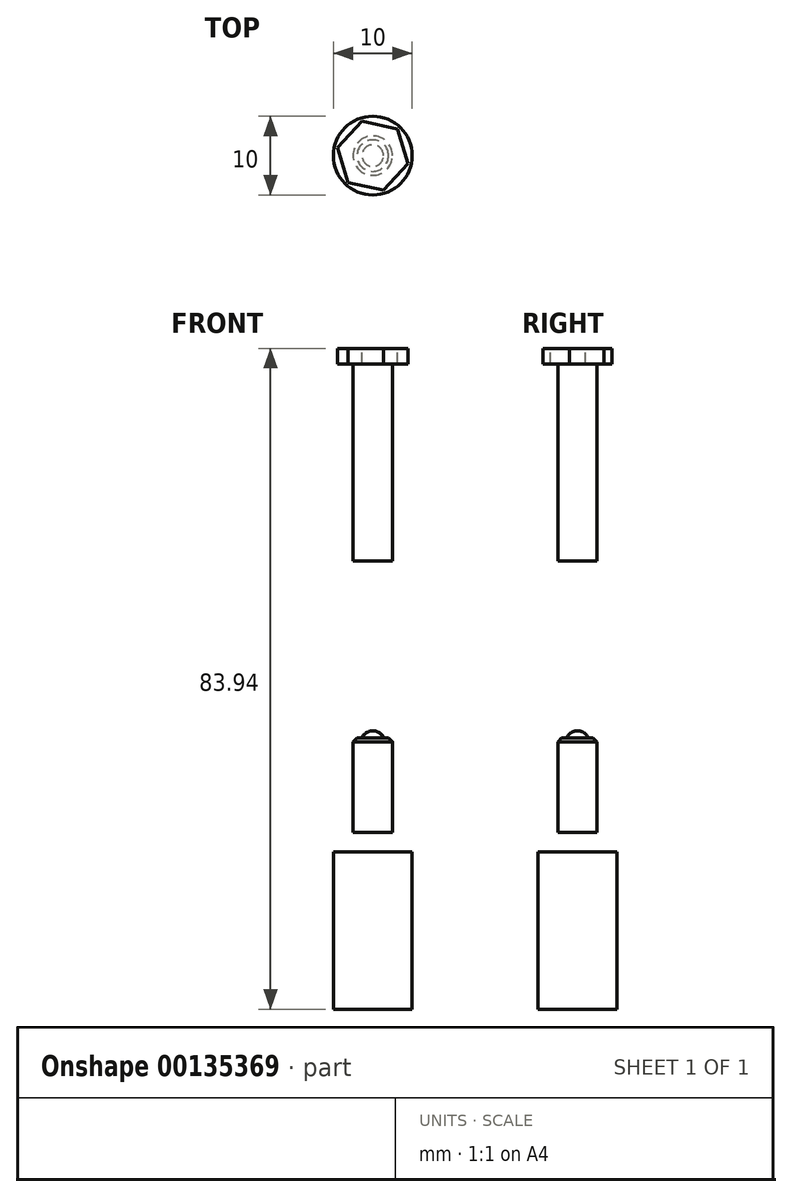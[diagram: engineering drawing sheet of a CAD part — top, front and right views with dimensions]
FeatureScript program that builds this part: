
annotation { "Feature Type Name" : "Feature", "Feature Type Description" : "" }
export const myFeature = defineFeature(function(context is Context, id is Id, definition is map)
    precondition{}
    {
        {
            var Q0;
            Q0=qCreatedBy(makeId("Front.planeOp"),FACE);
            var sketch = newSketch(context, id + "F0", { "sketchPlane" : qUnion([Q0])});
            skLineSegment(sketch, "E0", {"start": v(0, 0) * mm, "end": v(2.5, 0) * mm});
            skLineSegment(sketch, "E1", {"start": v(2.5, 0) * mm, "end": v(2.5, 25) * mm});
            skLineSegment(sketch, "E2", {"start": v(2.5, 25) * mm, "end": v(4, 25) * mm});
            skLineSegment(sketch, "E3", {"start": v(4, 25) * mm, "end": v(4, 27) * mm});
            skLineSegment(sketch, "E4", {"start": v(4, 27) * mm, "end": v(0, 27) * mm});
            skLineSegment(sketch, "E5", {"start": v(0, 27) * mm, "end": v(0, 0) * mm});
            skLineSegment(sketch, "E6", {"start": v(0, 0) * mm, "end": v(0, 27) * mm, "construction": true});
            skLineSegment(sketch, "E7.bottom", {"start": v(1.37, -22.46) * mm, "end": v(2.5, -22.46) * mm});
            skLineSegment(sketch, "E7.top", {"start": v(0, -34.46) * mm, "end": v(2.5, -34.46) * mm});
            skLineSegment(sketch, "E7.left", {"start": v(0, -22.46) * mm, "end": v(0, -34.46) * mm});
            skLineSegment(sketch, "E7.right", {"start": v(2.5, -22.46) * mm, "end": v(2.5, -34.46) * mm});
            skArc(sketch, "E8", {"start": v(1.37, -22.46) * mm, "mid": v(0.82, -21.8) * mm, "end": v(0, -21.56) * mm});
            skLineSegment(sketch, "E9", {"start": v(0, -22.46) * mm, "end": v(0, -21.56) * mm});
            skLineSegment(sketch, "E10.bottom", {"start": v(0, -36.94) * mm, "end": v(5, -36.94) * mm});
            skLineSegment(sketch, "E10.top", {"start": v(0, -56.94) * mm, "end": v(5, -56.94) * mm});
            skLineSegment(sketch, "E10.left", {"start": v(0, -36.94) * mm, "end": v(0, -56.94) * mm});
            skLineSegment(sketch, "E10.right", {"start": v(5, -36.94) * mm, "end": v(5, -56.94) * mm});
            skSolve(sketch);
        }
        {
            var Q0;
            Q0 = qSketchRegion(id + "F0", true);
            var Q1;
            Q1=sQuery(id+"F0.wireOp",EDGE,"E5");
            revolve(context, id + "F1", {"entities" : qUnion([Q0]), "axis" : qUnion([Q1]), "revolveType" : RevolveType.FULL});
        }
        {
            var Q0;
            Q0=makeQuery(id+"F1.opRevolve","SWEPT_FACE",FACE,{"disambiguationData":[OSD([sQuery(id+"F0.wireOp",EDGE,"E4")])]});
            var sketch = newSketch(context, id + "F2", { "sketchPlane" : qUnion([Q0])});
            skCircle(sketch, "E11.cCircle", {"center": v(0, 0) * mm, "radius": 4 * mm, "construction": true});
            skLineSegment(sketch, "E11.0", {"start": v(4.5, -1.01) * mm, "end": v(1.38, -4.4) * mm});
            skLineSegment(sketch, "E11.1", {"start": v(1.38, -4.4) * mm, "end": v(-3.13, -3.4) * mm});
            skLineSegment(sketch, "E11.2", {"start": v(-3.13, -3.4) * mm, "end": v(-4.5, 1.01) * mm});
            skLineSegment(sketch, "E11.3", {"start": v(-4.5, 1.01) * mm, "end": v(-1.38, 4.4) * mm});
            skLineSegment(sketch, "E11.4", {"start": v(-1.38, 4.4) * mm, "end": v(3.13, 3.4) * mm});
            skLineSegment(sketch, "E11.5", {"start": v(3.13, 3.4) * mm, "end": v(4.5, -1.01) * mm});
            skPoint(sketch, "E11.0.midPoint", {"position": v(2.94, -2.71) * mm});
            skSolve(sketch);
        }
        {
            var Q0;
            Q0 = qSketchRegion(id + "F2", true);
            extrude(context, id + "F3", {"entities" : qUnion([Q0]), "operationType" : NewBodyOperationType.ADD, "oppositeDirection" : true, "depth" : 2 * mm});
        }
        {
            var Q0;
            Q0=makeQuery(id+"F1.opRevolve","SWEPT_EDGE",EDGE,{"disambiguationData":[OSD([sQuery(id+"F0.wireOp",EDGE,"E7.bottom"),sQuery(id+"F0.wireOp",EDGE,"E7.right")])]});
            chamfer(context, id + "F4", {"entities" : qUnion([Q0]), "width" : 0.5 * mm, "tangentPropagation" : true});
        }
    });
